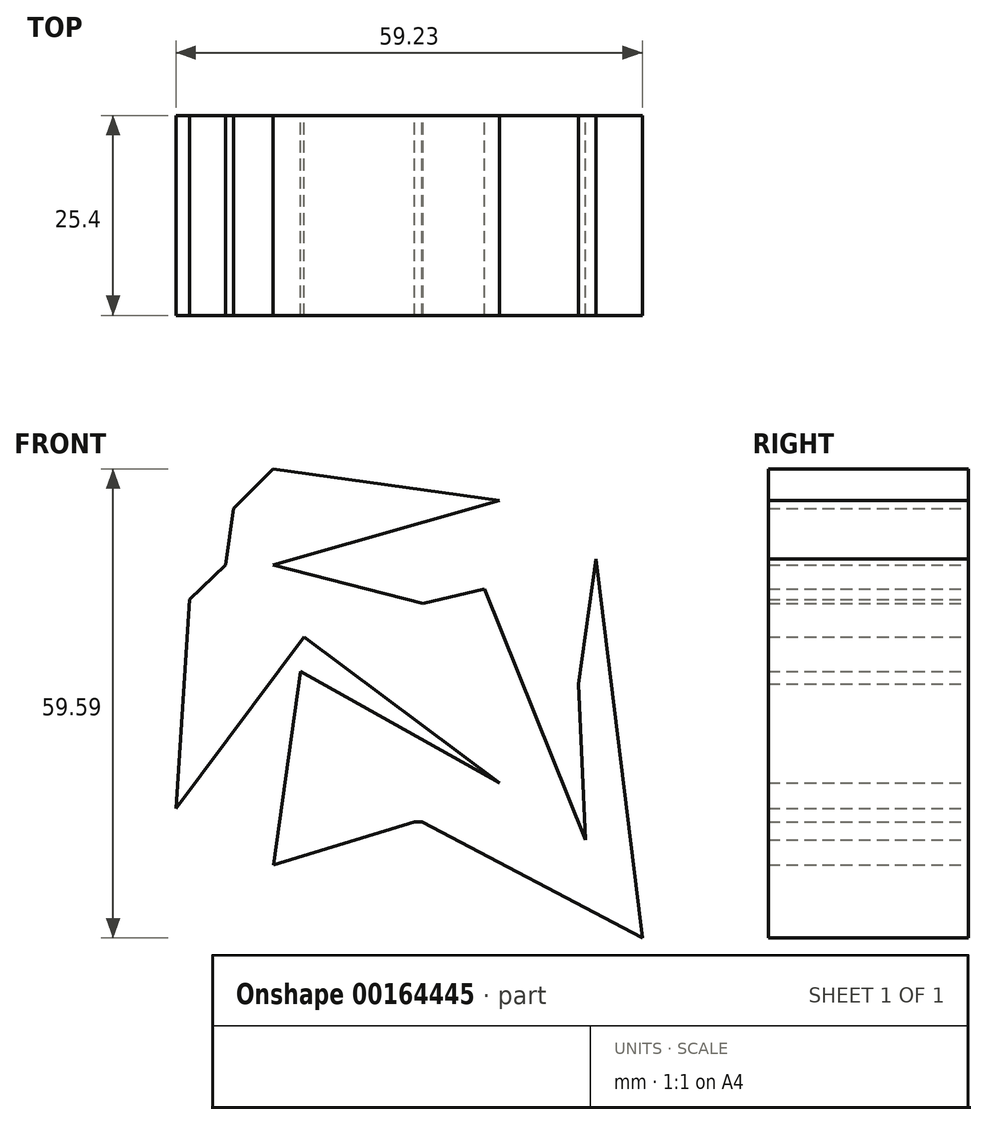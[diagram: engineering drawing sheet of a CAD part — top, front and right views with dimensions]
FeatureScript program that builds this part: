
annotation { "Feature Type Name" : "Feature", "Feature Type Description" : "" }
export const myFeature = defineFeature(function(context is Context, id is Id, definition is map)
    precondition{}
    {
        {
            var Q0;
            Q0=qCreatedBy(makeId("Front.planeOp"),FACE);
            var sketch = newSketch(context, id + "F0", { "sketchPlane" : qUnion([Q0])});
            skLineSegment(sketch, "E0", {"start": v(-20.14, 12.82) * mm, "end": v(-21.85, -13.68) * mm});
            skLineSegment(sketch, "E1", {"start": v(-21.85, -13.68) * mm, "end": v(-5.6, 8.06) * mm});
            skLineSegment(sketch, "E2", {"start": v(-6, 3.66) * mm, "end": v(-9.45, -20.9) * mm});
            skLineSegment(sketch, "E3", {"start": v(-5.6, 8.06) * mm, "end": v(19.22, -10.5) * mm});
            skLineSegment(sketch, "E4", {"start": v(-6, 3.66) * mm, "end": v(19.22, -10.5) * mm});
            skLineSegment(sketch, "E5", {"start": v(-9.45, -20.9) * mm, "end": v(8.44, -15.4) * mm});
            skLineSegment(sketch, "E6", {"start": v(9.42, -15.4) * mm, "end": v(37.38, -30.17) * mm});
            skLineSegment(sketch, "E7", {"start": v(37.38, -30.17) * mm, "end": v(31.51, 17.96) * mm});
            skLineSegment(sketch, "E8", {"start": v(31.51, 17.96) * mm, "end": v(29.3, 2.1) * mm});
            skLineSegment(sketch, "E9", {"start": v(29.3, 2.1) * mm, "end": v(30.18, -17.71) * mm});
            skLineSegment(sketch, "E10", {"start": v(30.18, -17.71) * mm, "end": v(17.35, 14.16) * mm});
            skLineSegment(sketch, "E11", {"start": v(17.35, 14.16) * mm, "end": v(9.54, 12.33) * mm});
            skLineSegment(sketch, "E12", {"start": v(9.54, 12.33) * mm, "end": v(-9.51, 17.21) * mm});
            skLineSegment(sketch, "E13", {"start": v(-9.51, 17.21) * mm, "end": v(19.22, 25.4) * mm});
            skLineSegment(sketch, "E14", {"start": v(19.22, 25.4) * mm, "end": v(-9.51, 29.42) * mm});
            skLineSegment(sketch, "E15", {"start": v(-9.51, 29.42) * mm, "end": v(-14.52, 24.42) * mm});
            skLineSegment(sketch, "E16", {"start": v(-14.52, 24.42) * mm, "end": v(-15.53, 17.21) * mm});
            skLineSegment(sketch, "E17", {"start": v(-15.53, 17.21) * mm, "end": v(-20.14, 12.82) * mm});
            skPoint(sketch, "E18.orphan", {"position": v(-10.98, -21.38) * mm});
            skPoint(sketch, "E19.orphan", {"position": v(-9.51, -21.38) * mm});
            skLineSegment(sketch, "E20", {"start": v(9.42, -15.4) * mm, "end": v(8.44, -15.4) * mm});
            skSolve(sketch);
        }
        {
            var Q0;
            Q0 = qSketchRegion(id + "F0", true);
            extrude(context, id + "F1", {"entities" : qUnion([Q0]), "depth" : 25.4 * mm});
        }
    });
